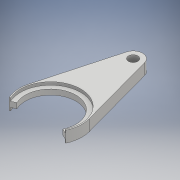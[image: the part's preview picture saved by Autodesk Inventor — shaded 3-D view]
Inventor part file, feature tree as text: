
AUTODESK INVENTOR PART (.ipt)
format: ipt  version: 2017 (Build 210142000, 142)  size: 146,944 bytes
history: native  units: mm
features: extrude x3, sketch x3, plane x1, mirror x1, projected_geometry x1
ambient origin geometry x8: Origin, YZ Plane, XZ Plane, XY Plane, X Axis, Y Axis, Z Axis, Center Point
bodies: Solid1 (feature_tree)
feature tree (9):
  extrude  "Extrusion1"  Depth=8.0mm
  extrude  "Extrusion2"  Depth=8.0mm
  plane  "Work Plane1"
  mirror  "Mirror1"
  extrude  "Extrusion3"  Depth=4.5mm TaperAngle=0.0deg
  sketch  "Sketch1"  dims[d0=43.0mm d1=8.0mm]
  sketch  "Sketch2"  dims[d2=70.0mm d3=8.0mm]
  projected_geometry  "Projected Loop1"
  sketch  "Sketch3"  dims[d4=5.0mm d5=4.5mm d6=0.0mm d7=51.0mm d8=2.5mm d9=0.0mm d10=22.68928mm d11=4.0mm d12=0.0mm]
